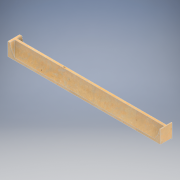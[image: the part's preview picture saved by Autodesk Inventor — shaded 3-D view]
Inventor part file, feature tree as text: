
AUTODESK INVENTOR PART (.ipt)
format: ipt  version: 2022.2 (Build 262287010, 287A)  size: 210,432 bytes
history: native  units: in
note: dims shown in document units (in); Inventor stores cm internally (conversion verified against a paired STEP export)
features: direct_edit x1, extrude x1, sketch x1, projected_geometry x1, revolve x1
ambient origin geometry x8: Origin, YZ Plane, XZ Plane, XY Plane, X Axis, Y Axis, Z Axis, Center Point
bodies: Solid1 (feature_tree), Body1 (feature_tree)
feature tree (5):
  direct_edit  "Direct Edit1"
  extrude  "Extrusion1"  Depth=0.375in TaperAngle=0.0deg
  sketch  "Sketch1"  dims[d0=180.0deg d1=0.375in d2=0.0in]
  projected_geometry  "Projected Loop1"
  revolve  "Rotate1"  [1 undecoded]
note: 1 required parameter value undecoded (feature->parameter linkage not recoverable at this tier; creation-order binding heuristic only, values carry confidence <= 0.55)
